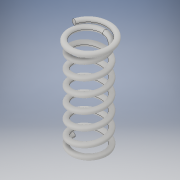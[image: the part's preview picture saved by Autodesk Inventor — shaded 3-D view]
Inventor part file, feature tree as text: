
AUTODESK INVENTOR PART (.ipt)
format: ipt  version: 2018 (Build 220112000, 112)  size: 539,136 bytes
history: native  units: in
note: dims shown in document units (in); Inventor stores cm internally (conversion verified against a paired STEP export)
features: sketch x3, helix x2
ambient origin geometry x8: Origin, YZ Plane, XZ Plane, XY Plane, X Axis, Y Axis, Z Axis, Center Point
bodies: Solid1 (feature_tree)
feature tree (5):
  helix  "Coil1"  [1 undecoded]
  helix  "Coil2"  [1 undecoded]
  sketch  "Sketch3"
  sketch  "Sketch1"  dims[d2=1.0in d3=0.35in d4=2.3622in d5=0.0in d6=90.0deg d7=180.0deg d8=0.0in d9=0.0in]
  sketch  "Sketch2"  dims[d10=1.0in d11=0.016in d12=0.3937in d13=0.3436in d14=0.0in d15=0.0in d16=75.0deg d17=0.0in]
note: 2 required parameter values undecoded (feature->parameter linkage not recoverable at this tier; creation-order binding heuristic only, values carry confidence <= 0.55)
